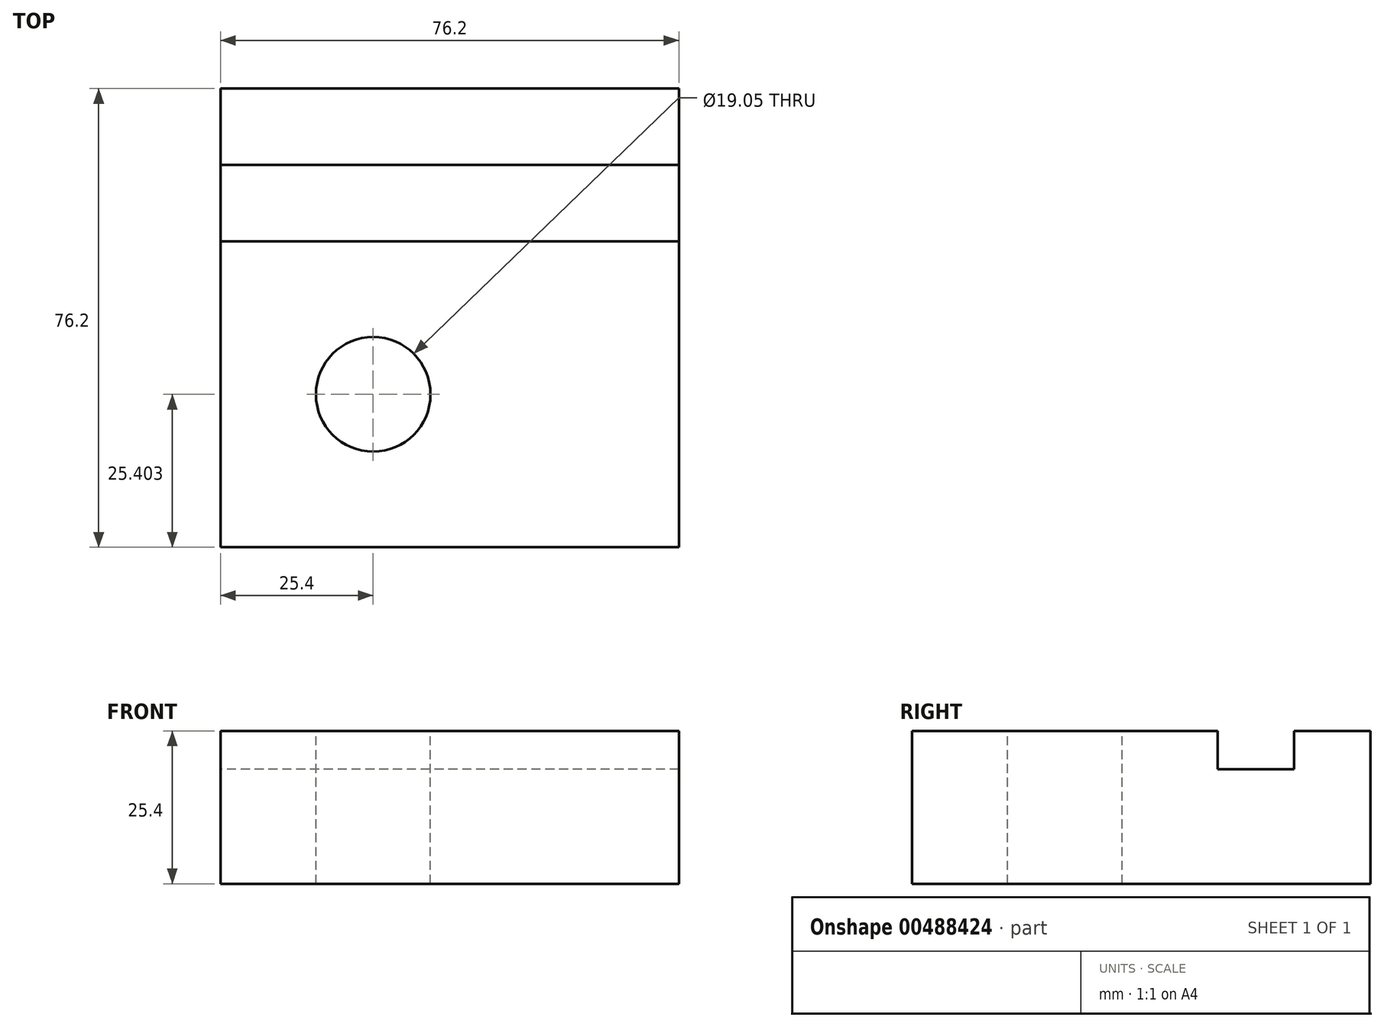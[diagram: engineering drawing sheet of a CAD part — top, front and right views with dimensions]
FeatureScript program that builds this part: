
annotation { "Feature Type Name" : "Feature", "Feature Type Description" : "" }
export const myFeature = defineFeature(function(context is Context, id is Id, definition is map)
    precondition{}
    {
        {
            var Q0;
            Q0=qCreatedBy(makeId("Right.planeOp"),FACE);
            var sketch = newSketch(context, id + "F0", { "sketchPlane" : qUnion([Q0])});
            skLineSegment(sketch, "E0", {"start": v(-84.8, 27.8) * mm, "end": v(-84.8, 2.4) * mm});
            skLineSegment(sketch, "E1", {"start": v(-84.8, 2.4) * mm, "end": v(-8.6, 2.4) * mm});
            skLineSegment(sketch, "E2", {"start": v(-8.6, 2.4) * mm, "end": v(-8.6, 27.8) * mm});
            skLineSegment(sketch, "E3", {"start": v(-8.6, 27.8) * mm, "end": v(-21.3, 27.8) * mm});
            skLineSegment(sketch, "E4", {"start": v(-21.3, 27.8) * mm, "end": v(-21.3, 21.46) * mm});
            skLineSegment(sketch, "E5", {"start": v(-21.3, 21.46) * mm, "end": v(-34, 21.46) * mm});
            skLineSegment(sketch, "E6", {"start": v(-34, 21.46) * mm, "end": v(-34, 27.8) * mm});
            skLineSegment(sketch, "E7", {"start": v(-34, 27.8) * mm, "end": v(-84.8, 27.8) * mm});
            skSolve(sketch);
        }
        {
            var Q0;
            Q0 = qSketchRegion(id + "F0", true);
            extrude(context, id + "F1", {"entities" : qUnion([Q0]), "depth" : 76.2 * mm});
        }
        {
            var Q0;
            Q0=makeQuery(id+"F1.opExtrude","SWEPT_FACE",FACE,{"disambiguationData":[OSD([sQuery(id+"F0.wireOp",EDGE,"E7")])]});
            var sketch = newSketch(context, id + "F2", { "sketchPlane" : qUnion([Q0])});
            skLineSegment(sketch, "E8", {"start": v(-16.59, -59.4) * mm, "end": v(42.65, -59.4) * mm, "construction": true});
            skLineSegment(sketch, "E9", {"start": v(25.4, -105.43) * mm, "end": v(25.4, -46.23) * mm, "construction": true});
            skCircle(sketch, "E10", {"center": v(25.4, -59.4) * mm, "radius": 9.53 * mm});
            skSolve(sketch);
        }
        {
            var Q0;
            Q0 = qSketchRegion(id + "F2", true);
            extrude(context, id + "F3", {"entities" : qUnion([Q0]), "operationType" : NewBodyOperationType.REMOVE, "endBound" : BoundingType.THROUGH_ALL, "oppositeDirection" : true, "depth" : 25.4 * mm});
        }
    });
